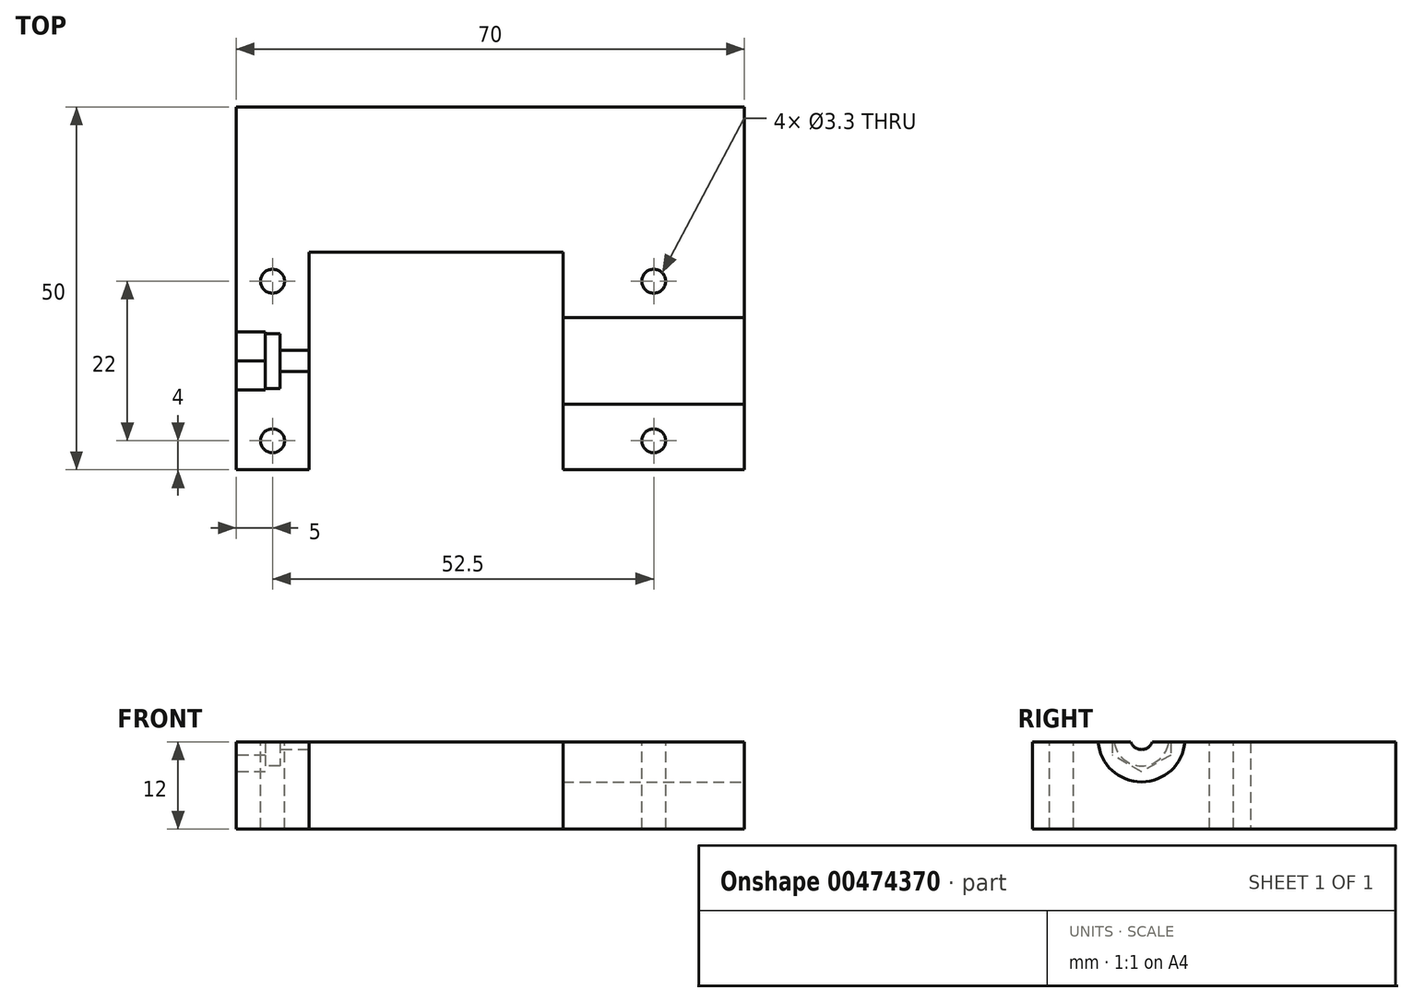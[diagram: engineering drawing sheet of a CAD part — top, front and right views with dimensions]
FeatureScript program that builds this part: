
annotation { "Feature Type Name" : "Feature", "Feature Type Description" : "" }
export const myFeature = defineFeature(function(context is Context, id is Id, definition is map)
    precondition{}
    {
        {
            var Q0;
            Q0=qCreatedBy(makeId("Top.planeOp"),FACE);
            var sketch = newSketch(context, id + "F0", { "sketchPlane" : qUnion([Q0])});
            skLineSegment(sketch, "E0.bottom", {"start": v(-35, -25) * mm, "end": v(35, -25) * mm});
            skLineSegment(sketch, "E0.top", {"start": v(-35, 25) * mm, "end": v(35, 25) * mm});
            skLineSegment(sketch, "E0.left", {"start": v(-35, -25) * mm, "end": v(-35, 25) * mm});
            skLineSegment(sketch, "E0.right", {"start": v(35, -25) * mm, "end": v(35, 25) * mm});
            skPoint(sketch, "E0.middle", {"position": v(0, 0) * mm});
            skSolve(sketch);
        }
        {
            var Q0;
            Q0=qSketchRegion(id+"F0",true);
            extrude(context, id + "F1", {"entities" : qUnion([Q0]), "depth" : 30 * mm});
        }
        {
            var Q0;
            Q0=makeQuery(id+"F1.opExtrude","SWEPT_FACE",FACE,{"disambiguationData":[OSD([sQuery(id+"F0.wireOp",EDGE,"E0.left")])]});
            var sketch = newSketch(context, id + "F2", { "sketchPlane" : qUnion([Q0])});
            skPoint(sketch, "E1.endSnap0", {"position": v(0, 0) * mm});
            skLineSegment(sketch, "E2", {"start": v(-25, 15) * mm, "end": v(-5, 15) * mm, "construction": true});
            skLineSegment(sketch, "E3", {"start": v(25, 0) * mm, "end": v(25, 12.5) * mm, "construction": true});
            skLineSegment(sketch, "E4", {"start": v(25, 12.5) * mm, "end": v(10, 12.5) * mm, "construction": true});
            skLineSegment(sketch, "E5", {"start": v(10, 12.5) * mm, "end": v(10, 17.12) * mm, "construction": true});
            skLineSegment(sketch, "E6", {"start": v(10, 12.5) * mm, "end": v(14, 14.81) * mm, "construction": true});
            skLineSegment(sketch, "E7.MirrorCS", {"start": v(10, 12.5) * mm, "end": v(14, 10.2) * mm, "construction": true});
            skLineSegment(sketch, "E8.MirrorCS", {"start": v(10, 12.5) * mm, "end": v(10, 7.88) * mm, "construction": true});
            skLineSegment(sketch, "E9.MirrorCS", {"start": v(10, 12.5) * mm, "end": v(6, 10.19) * mm, "construction": true});
            skLineSegment(sketch, "E10.MirrorCS", {"start": v(10, 12.5) * mm, "end": v(6, 14.8) * mm, "construction": true});
            skLineSegment(sketch, "E11", {"start": v(6, 14.8) * mm, "end": v(10, 17.12) * mm});
            skLineSegment(sketch, "E12", {"start": v(6, 14.8) * mm, "end": v(6, 10.19) * mm});
            skLineSegment(sketch, "E13", {"start": v(6, 10.19) * mm, "end": v(10, 7.88) * mm});
            skLineSegment(sketch, "E14", {"start": v(10, 7.88) * mm, "end": v(14, 10.2) * mm});
            skLineSegment(sketch, "E15", {"start": v(14, 14.81) * mm, "end": v(14, 10.2) * mm});
            skLineSegment(sketch, "E16", {"start": v(14, 14.81) * mm, "end": v(10, 17.12) * mm});
            skLineSegment(sketch, "E17", {"start": v(6, 14.8) * mm, "end": v(14, 14.81) * mm, "construction": true});
            skSolve(sketch);
        }
        {
            var Q0;
            Q0=qCreatedBy(makeId("Top.planeOp"),FACE);
            var sketch = newSketch(context, id + "F3", { "sketchPlane" : qUnion([Q0])});
            skLineSegment(sketch, "E18", {"start": v(0, 0) * mm, "end": v(0, 5) * mm, "construction": true});
            skLineSegment(sketch, "E19", {"start": v(0, 0) * mm, "end": v(0, -25) * mm, "construction": true});
            skLineSegment(sketch, "E20", {"start": v(0, 0) * mm, "end": v(10, 0) * mm, "construction": true});
            skLineSegment(sketch, "E21", {"start": v(0, 0) * mm, "end": v(-25, 0) * mm, "construction": true});
            skLineSegment(sketch, "E22", {"start": v(10, 0) * mm, "end": v(10, 5) * mm});
            skLineSegment(sketch, "E23", {"start": v(0, 5) * mm, "end": v(10, 5) * mm});
            skLineSegment(sketch, "E24", {"start": v(10, 0) * mm, "end": v(10, -25) * mm});
            skLineSegment(sketch, "E25", {"start": v(0, 5) * mm, "end": v(-25, 5) * mm});
            skLineSegment(sketch, "E26", {"start": v(-25, 5) * mm, "end": v(-25, -25) * mm});
            skLineSegment(sketch, "E27", {"start": v(0, -25) * mm, "end": v(-25, -25) * mm, "construction": true});
            skLineSegment(sketch, "E28", {"start": v(0, -25) * mm, "end": v(74.72, -25) * mm, "construction": true});
            skLineSegment(sketch, "E29", {"start": v(-25, -25) * mm, "end": v(10, -25) * mm});
            skSolve(sketch);
        }
        {
            var Q0;
            Q0=qSketchRegion(id+"F3",true);
            var Q1;
            Q1=makeQuery(id+"F1.opExtrude","CAP_FACE",FACE,{"disambiguationData":[OSD([sQuery(id+"F0.wireOp",EDGE,"E0.bottom"),sQuery(id+"F0.wireOp",EDGE,"E0.top"),sQuery(id+"F0.wireOp",EDGE,"E0.left"),sQuery(id+"F0.wireOp",EDGE,"E0.right")])],"isStart":false});
            extrude(context, id + "F4", {"entities" : qUnion([Q0]), "operationType" : NewBodyOperationType.REMOVE, "endBound" : BoundingType.UP_TO_SURFACE, "endBoundEntityFace" : qUnion([Q1]), "depth" : 25 * mm});
        }
        {
            var Q0;
            Q0=qSketchRegion(id+"F2",true);
            extrude(context, id + "F5", {"entities" : qUnion([Q0]), "operationType" : NewBodyOperationType.REMOVE, "oppositeDirection" : true, "depth" : 4 * mm});
        }
        {
            var Q0;
            Q0=makeQuery(id+"F5.boolean.opBoolean","COPY",FACE,{"derivedFrom":makeQuery(id+"F5.opExtrude","CAP_FACE",FACE,{"disambiguationData":[OSD([sQuery(id+"F2.wireOp",EDGE,"E11"),sQuery(id+"F2.wireOp",EDGE,"E12"),sQuery(id+"F2.wireOp",EDGE,"E13"),sQuery(id+"F2.wireOp",EDGE,"E14"),sQuery(id+"F2.wireOp",EDGE,"E15"),sQuery(id+"F2.wireOp",EDGE,"E16")])],"isStart":false})});
            var sketch = newSketch(context, id + "F6", { "sketchPlane" : qUnion([Q0])});
            skCircle(sketch, "E30", {"center": v(10, 12.5) * mm, "radius": 3.8 * mm});
            skLineSegment(sketch, "E31", {"start": v(0, 0) * mm, "end": v(10, 0) * mm, "construction": true});
            skLineSegment(sketch, "E32", {"start": v(10, 0) * mm, "end": v(10, 12.5) * mm, "construction": true});
            skSolve(sketch);
        }
        {
            var Q0;
            Q0=qSketchRegion(id+"F6",true);
            extrude(context, id + "F7", {"entities" : qUnion([Q0]), "operationType" : NewBodyOperationType.REMOVE, "oppositeDirection" : true, "depth" : 2 * mm});
        }
        {
            var Q0;
            Q0=makeQuery(id+"F7.boolean.opBoolean","COPY",FACE,{"derivedFrom":makeQuery(id+"F7.opExtrude","CAP_FACE",FACE,{"disambiguationData":[OSD([sQuery(id+"F6.wireOp",EDGE,"E30")])],"isStart":false})});
            var sketch = newSketch(context, id + "F8", { "sketchPlane" : qUnion([Q0])});
            skLineSegment(sketch, "E33", {"start": v(10, 20.63) * mm, "end": v(10, 4.75) * mm, "construction": true});
            skLineSegment(sketch, "E34", {"start": v(3.02, 8.45) * mm, "end": v(16.9, 16.52) * mm, "construction": true});
            skCircle(sketch, "E35", {"center": v(10, 12.5) * mm, "radius": 1.55 * mm});
            skSolve(sketch);
        }
        {
            var Q0;
            Q0=qSketchRegion(id+"F8",true);
            extrude(context, id + "F9", {"entities" : qUnion([Q0]), "operationType" : NewBodyOperationType.REMOVE, "oppositeDirection" : true, "depth" : 7 * mm});
        }
        {
            var Q0;
            Q0=makeQuery(id+"F1.opExtrude","SWEPT_FACE",FACE,{"disambiguationData":[OSD([sQuery(id+"F0.wireOp",EDGE,"E0.right")])]});
            var sketch = newSketch(context, id + "F10", { "sketchPlane" : qUnion([Q0])});
            skLineSegment(sketch, "E36", {"start": v(-25, 0) * mm, "end": v(-25, 12.5) * mm, "construction": true});
            skLineSegment(sketch, "E37", {"start": v(-25, 12.5) * mm, "end": v(-10, 12.5) * mm, "construction": true});
            skCircle(sketch, "E38", {"center": v(-10, 12.5) * mm, "radius": 6 * mm});
            skSolve(sketch);
        }
        {
            var Q0;
            Q0=makeQuery(id+"F1.opExtrude","SWEPT_FACE",FACE,{"disambiguationData":[OSD([sQuery(id+"F0.wireOp",EDGE,"E0.top")])]});
            var sketch = newSketch(context, id + "F11", { "sketchPlane" : qUnion([Q0])});
            skPoint(sketch, "E39.endSnap0", {"position": v(0, 0) * mm});
            skLineSegment(sketch, "E40", {"start": v(65, 6) * mm, "end": v(90, 6) * mm, "construction": true});
            skCircle(sketch, "E41", {"center": v(90, 6) * mm, "radius": 0.5 * mm});
            skLineSegment(sketch, "E42", {"start": v(0, 0) * mm, "end": v(-5, 0) * mm, "construction": true});
            skLineSegment(sketch, "E43", {"start": v(0, 0) * mm, "end": v(0, 6) * mm, "construction": true});
            skCircle(sketch, "E44", {"center": v(65, 6) * mm, "radius": 0.5 * mm});
            skLineSegment(sketch, "E45", {"start": v(65, 6) * mm, "end": v(-35, 6) * mm, "construction": true});
            skSolve(sketch);
        }
        {
            var Q0;
            Q0=qSketchRegion(id+"F10",true);
            var Q1;
            Q1=makeQuery(id+"F4.boolean.opBoolean","COPY",FACE,{"derivedFrom":makeQuery(id+"F4.opExtrude","SWEPT_FACE",FACE,{"disambiguationData":[OSD([sQuery(id+"F3.wireOp",EDGE,"E22"),sQuery(id+"F3.wireOp",EDGE,"E24")])]})});
            extrude(context, id + "F12", {"entities" : qUnion([Q0]), "operationType" : NewBodyOperationType.REMOVE, "endBound" : BoundingType.UP_TO_SURFACE, "oppositeDirection" : true, "endBoundEntityFace" : qUnion([Q1]), "depth" : 25 * mm});
        }
        {
            var Q0;
            Q0=qSketchRegion(id+"F11",true);
            var Q1;
            Q1=makeQuery(id+"F4.boolean.opBoolean","COPY",FACE,{"derivedFrom":makeQuery(id+"F4.opExtrude","SWEPT_FACE",FACE,{"disambiguationData":[OSD([sQuery(id+"F3.wireOp",EDGE,"YkLpMczh-LnJE-8Oms-Y8Ta-dxZD4QefJqg7")])]})});
            extrude(context, id + "F13", {"entities" : qUnion([Q0]), "operationType" : NewBodyOperationType.REMOVE, "oppositeDirection" : true, "endBoundEntityFace" : qUnion([Q1]), "depth" : 1 * mm});
        }
        {
            var Q0;
            Q0=makeQuery(id+"F1.opExtrude","CAP_FACE",FACE,{"disambiguationData":[OSD([sQuery(id+"F0.wireOp",EDGE,"E0.bottom"),sQuery(id+"F0.wireOp",EDGE,"E0.top"),sQuery(id+"F0.wireOp",EDGE,"E0.left"),sQuery(id+"F0.wireOp",EDGE,"E0.right")])],"isStart":false});
            var sketch = newSketch(context, id + "F14", { "sketchPlane" : qUnion([Q0])});
            skLineSegment(sketch, "E46.bottom", {"start": v(-35, -25) * mm, "end": v(35, -25) * mm});
            skLineSegment(sketch, "E46.top", {"start": v(-35, 25) * mm, "end": v(35, 25) * mm});
            skLineSegment(sketch, "E46.left", {"start": v(-35, -25) * mm, "end": v(-35, 25) * mm});
            skLineSegment(sketch, "E46.right", {"start": v(35, -25) * mm, "end": v(35, 25) * mm});
            skSolve(sketch);
        }
        {
            var Q0;
            Q0=qSketchRegion(id+"F14",true);
            extrude(context, id + "F15", {"entities" : qUnion([Q0]), "operationType" : NewBodyOperationType.REMOVE, "oppositeDirection" : true, "depth" : 18 * mm});
        }
        {
            var Q0;
            {var subQ0=sQuery(id+"F2.wireOp",EDGE,"E12");var subQ1=sQuery(id+"F6.wireOp",EDGE,"E30");Q0=makeQuery(id+"F15.boolean.opBoolean","COPY",FACE,{"disambiguationData":[TD([makeQuery(id+"F1.opExtrude","SWEPT_FACE",FACE,{"disambiguationData":[OSD([sQuery(id+"F0.wireOp",EDGE,"E0.top")])]}),makeQuery(id+"F1.opExtrude","SWEPT_FACE",FACE,{"disambiguationData":[OSD([sQuery(id+"F0.wireOp",EDGE,"E0.left")])]}),makeQuery(id+"F1.opExtrude","SWEPT_FACE",FACE,{"disambiguationData":[OSD([sQuery(id+"F0.wireOp",EDGE,"E0.right")])]}),makeQuery(id+"F4.boolean.opBoolean","COPY",FACE,{"derivedFrom":makeQuery(id+"F4.opExtrude","SWEPT_FACE",FACE,{"disambiguationData":[OSD([sQuery(id+"F3.wireOp",EDGE,"YkLpMczh-LnJE-8Oms-Y8Ta-dxZD4QefJqg7")])]})}),makeQuery(id+"F4.boolean.opBoolean","COPY",FACE,{"derivedFrom":makeQuery(id+"F4.opExtrude","SWEPT_FACE",FACE,{"disambiguationData":[OSD([sQuery(id+"F3.wireOp",EDGE,"0GEvvDHn-DFwf-QAS0-vYnM-1EEuX2mMo1AG")])]})}),makeQuery(id+"F4.boolean.opBoolean","COPY",FACE,{"derivedFrom":makeQuery(id+"F4.opExtrude","SWEPT_FACE",FACE,{"disambiguationData":[OSD([sQuery(id+"F3.wireOp",EDGE,"liEGX8ho-NAPC-Z8Vj-w4bI-YO61ROXNVXDp")])]})}),makeQuery(id+"F5.boolean.opBoolean","COPY",FACE,{"derivedFrom":makeQuery(id+"F5.opExtrude","CAP_FACE",FACE,{"disambiguationData":[OSD([sQuery(id+"F2.wireOp",EDGE,"E11"),subQ0,sQuery(id+"F2.wireOp",EDGE,"E13"),sQuery(id+"F2.wireOp",EDGE,"E14"),sQuery(id+"F2.wireOp",EDGE,"E15"),sQuery(id+"F2.wireOp",EDGE,"E16")])],"isStart":false})}),makeQuery(id+"F5.boolean.opBoolean","COPY",FACE,{"derivedFrom":makeQuery(id+"F5.opExtrude","SWEPT_FACE",FACE,{"disambiguationData":[OSD([subQ0])]})}),makeQuery(id+"F7.boolean.opBoolean","COPY",FACE,{"derivedFrom":makeQuery(id+"F7.opExtrude","SWEPT_FACE",FACE,{"disambiguationData":[OSD([subQ1])]})}),makeQuery(id+"F7.boolean.opBoolean","COPY",FACE,{"derivedFrom":makeQuery(id+"F7.opExtrude","CAP_FACE",FACE,{"disambiguationData":[OSD([subQ1])],"isStart":false})}),makeQuery(id+"F9.boolean.opBoolean","COPY",FACE,{"derivedFrom":makeQuery(id+"F9.opExtrude","SWEPT_FACE",FACE,{"disambiguationData":[OSD([sQuery(id+"F8.wireOp",EDGE,"E35")])]})}),makeQuery(id+"F12.boolean.opBoolean","COPY",FACE,{"derivedFrom":makeQuery(id+"F12.opExtrude","SWEPT_FACE",FACE,{"disambiguationData":[OSD([sQuery(id+"F10.wireOp",EDGE,"E38")])]})})])],"derivedFrom":makeQuery(id+"F15.opExtrude","CAP_FACE",FACE,{"disambiguationData":[OSD([sQuery(id+"F14.wireOp",EDGE,"E46.bottom"),sQuery(id+"F14.wireOp",EDGE,"E46.top"),sQuery(id+"F14.wireOp",EDGE,"E46.left"),sQuery(id+"F14.wireOp",EDGE,"E46.right")])],"isStart":false})});}
            var sketch = newSketch(context, id + "F16", { "sketchPlane" : qUnion([Q0])});
            skPoint(sketch, "E47.middle", {"position": v(0, 0) * mm});
            skLineSegment(sketch, "E48.bottom", {"start": v(35, -25) * mm, "end": v(-35, -25) * mm, "construction": true});
            skLineSegment(sketch, "E48.top", {"start": v(35, 25) * mm, "end": v(-35, 25) * mm, "construction": true});
            skLineSegment(sketch, "E48.left", {"start": v(35, -25) * mm, "end": v(35, 25) * mm, "construction": true});
            skLineSegment(sketch, "E48.right", {"start": v(-35, -25) * mm, "end": v(-35, 25) * mm, "construction": true});
            skLineSegment(sketch, "E49", {"start": v(-35, -25) * mm, "end": v(-30, -25) * mm, "construction": true});
            skLineSegment(sketch, "E50", {"start": v(-30, -25) * mm, "end": v(-30, -10) * mm, "construction": true});
            skLineSegment(sketch, "E51", {"start": v(-30, -10) * mm, "end": v(22.5, -10) * mm, "construction": true});
            skLineSegment(sketch, "E52", {"start": v(22.5, -10) * mm, "end": v(22.5, -25) * mm, "construction": true});
            skLineSegment(sketch, "E53", {"start": v(22.5, -10) * mm, "end": v(22.5, 1) * mm, "construction": true});
            skLineSegment(sketch, "E54", {"start": v(22.5, -10) * mm, "end": v(22.5, -21) * mm, "construction": true});
            skCircle(sketch, "E55", {"center": v(22.5, 1) * mm, "radius": 1.65 * mm});
            skCircle(sketch, "E56", {"center": v(22.5, -21) * mm, "radius": 1.65 * mm});
            skLineSegment(sketch, "E57", {"start": v(-30, -10) * mm, "end": v(-30, 1) * mm, "construction": true});
            skLineSegment(sketch, "E58", {"start": v(-30, -10) * mm, "end": v(-30, -21) * mm, "construction": true});
            skCircle(sketch, "E59", {"center": v(-30, 1) * mm, "radius": 1.65 * mm});
            skCircle(sketch, "E60", {"center": v(-30, -21) * mm, "radius": 1.65 * mm});
            skSolve(sketch);
        }
        {
            var Q0;
            Q0=qSketchRegion(id+"F16",true);
            var Q1;
            Q1=makeQuery(id+"F1.opExtrude","CAP_FACE",FACE,{"disambiguationData":[OSD([sQuery(id+"F0.wireOp",EDGE,"E0.bottom"),sQuery(id+"F0.wireOp",EDGE,"E0.top"),sQuery(id+"F0.wireOp",EDGE,"E0.left"),sQuery(id+"F0.wireOp",EDGE,"E0.right")])],"isStart":true});
            extrude(context, id + "F17", {"entities" : qUnion([Q0]), "operationType" : NewBodyOperationType.REMOVE, "endBound" : BoundingType.UP_TO_SURFACE, "oppositeDirection" : true, "endBoundEntityFace" : qUnion([Q1]), "depth" : 25 * mm});
        }
    });
